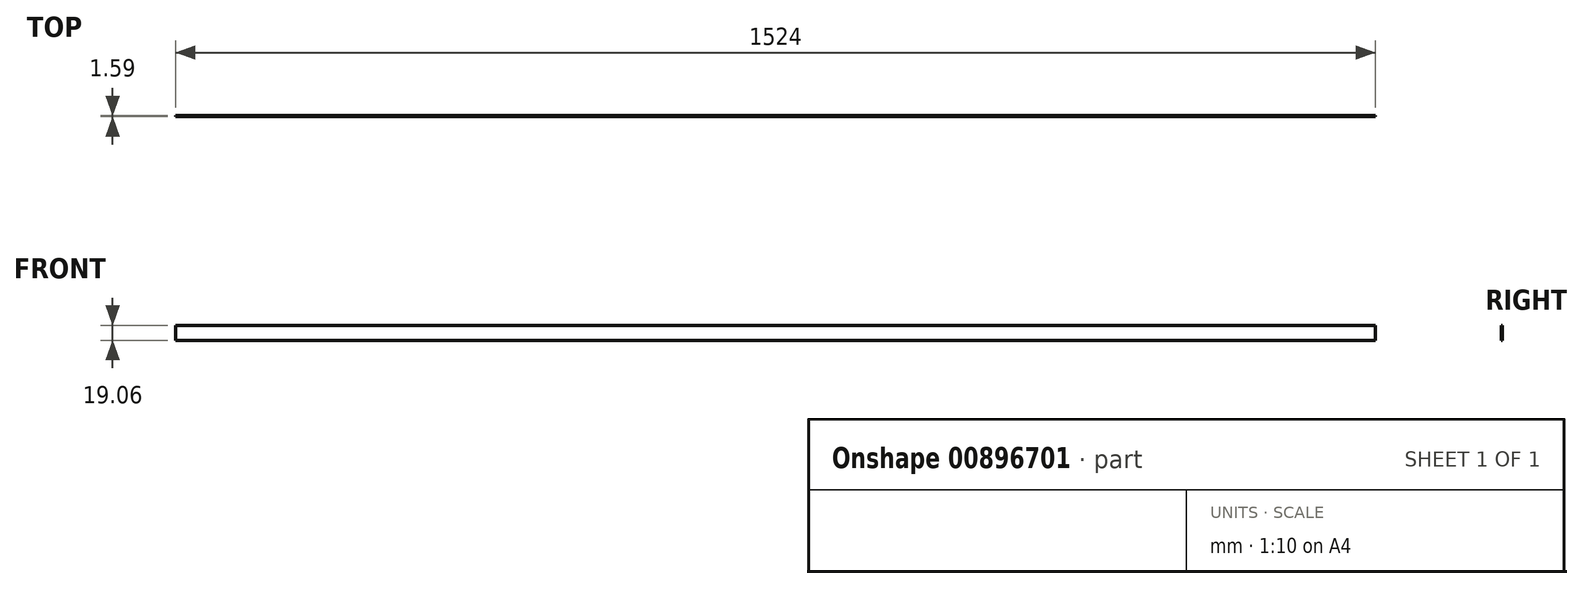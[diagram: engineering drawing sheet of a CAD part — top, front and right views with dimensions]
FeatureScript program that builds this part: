
annotation { "Feature Type Name" : "Feature", "Feature Type Description" : "" }
export const myFeature = defineFeature(function(context is Context, id is Id, definition is map)
    precondition{}
    {
        {
            var Q0;
            Q0=qCreatedBy(makeId("Front.planeOp"),FACE);
            var sketch = newSketch(context, id + "F0", { "sketchPlane" : qUnion([Q0])});
            skLineSegment(sketch, "E0.bottom", {"start": v(762, 9.52) * mm, "end": v(-762, 9.52) * mm});
            skLineSegment(sketch, "E0.top", {"start": v(762, -9.53) * mm, "end": v(-762, -9.53) * mm});
            skLineSegment(sketch, "E0.left", {"start": v(762, 9.52) * mm, "end": v(762, -9.53) * mm});
            skLineSegment(sketch, "E0.right", {"start": v(-762, 9.52) * mm, "end": v(-762, -9.53) * mm});
            skPoint(sketch, "E0.middle", {"position": v(0, 0) * mm});
            skSolve(sketch);
        }
        {
            var Q0;
            Q0=makeQuery(id+"F0.imprint","IMPRINT",FACE,{"disambiguationData":[TD([[makeQuery(id+"F0.imprint","IMPRINT",EDGE,{"derivedFrom":sQuery(id+"F0.wireOp",EDGE,"E0.bottom")}),1.0]])]});
            extrude(context, id + "F1", {"entities" : qUnion([Q0]), "depth" : 1.59 * mm, "offsetDistance" : 25.4 * mm});
        }
    });
